# Revit family: 306_eeb4c68d981f462b976296043c77c6
name_source: partatom
category: Pipe Accessories
units: mm (PartAtom-declared; Revit-internal decimal feet)

## family parameters
Always vertical = Yes
Cut with Voids When Loaded = No
Part Type = Valve - Breaks Into
Round Connector Dimension = Use Diameter
Shared = No
Work Plane-Based = No

## types (2) — shared parameters
CAT0 = Yes
Description = 3-way Motorized ball valve MBA136, PN32 internal/2x external thread
H1 = 1 mm  [stored 0.00328084 ft]
L2D_Min = 3048 mm
MC = No
Manufacturer = ESBE
QmdConnectorList = 301;D;302;D
RR = 4 mm  [stored 0.0131234 ft]
URL = http://www.esbe.eu
X14 = 3 mm  [stored 0.00984252 ft]
X15 = 8 mm  [stored 0.0262467 ft]
X15__ve = -8 mm
X16 = 5 mm  [stored 0.0164042 ft]
X5 = 3 mm  [stored 0.00984252 ft]
X5__ve = -3 mm
Y0 = 5 mm  [stored 0.0164042 ft]
Y11 = 3 mm  [stored 0.00984252 ft]
Z3 = 10 mm  [stored 0.0328084 ft]
Z4 = 55 mm
Z5 = 3 mm  [stored 0.00984252 ft]
Z6 = 35 mm
Z6__ve = -35 mm
magiPartTypeId = 306
magiProductFamilyId = eeb4c68d981f462b976296043c77c6

## per-type parameters (varying)
- MBA136 G1  MFM 230VAC 2-P 10NM: CenSd_Y13_6=15 mm  [stored 0.0492126 ft]; D=25 mm; E=29 mm  [stored 0.0951444 ft]; G=76 mm; H=73 mm; L2D=107 mm; W2D=25 mm  [stored 0.082021 ft]; X1=58 mm; X12=19 mm; X12__ve=-19 mm; X13=7 mm  [stored 0.0229659 ft]; X18=52 mm; X19=20 mm  [stored 0.0656168 ft]; X19__ve=-20 mm; X6=21 mm; Y1=13 mm  [stored 0.0426509 ft]; Y10=16 mm; Y10__ve=-16 mm  [stored -0.0524934 ft]; Y12=14 mm  [stored 0.0459318 ft]; Y13=18 mm; Y14=9 mm  [stored 0.0295276 ft]; Y15=17 mm; Y2=13 mm  [stored 0.0426509 ft]; Y3=13 mm  [stored 0.0426509 ft]; Y4=15 mm  [stored 0.0492126 ft]; Y5=15 mm  [stored 0.0492126 ft]; Z10=34 mm; Z2=26 mm; Z2__ve=-26 mm; Z8=16 mm; magiProductCode=MBA136 G1" MFM 230VAC 2-P 10NM; magiProductId=84465b65f17d4973b765fd3aec1b71
- MBA136 G3/4  MFM 230VAC 2-P 10NM: CenSd_Y13_6=12 mm  [stored 0.0393701 ft]; D=20 mm; E=25 mm  [stored 0.082021 ft]; G=70 mm; H=65 mm; L2D=91 mm; W2D=20 mm  [stored 0.0656168 ft]; X1=50 mm  [stored 0.164042 ft]; X12=16 mm; X12__ve=-16 mm  [stored -0.0524934 ft]; X13=6 mm  [stored 0.019685 ft]; X18=45 mm; X19=17 mm; X19__ve=-17 mm; X6=19 mm; Y1=10 mm  [stored 0.0328084 ft]; Y10=13 mm  [stored 0.0426509 ft]; Y10__ve=-13 mm  [stored -0.0426509 ft]; Y12=11 mm; Y13=14 mm  [stored 0.0459318 ft]; Y14=7 mm  [stored 0.0229659 ft]; Y15=13 mm  [stored 0.0426509 ft]; Y2=10 mm  [stored 0.0328084 ft]; Y3=11 mm; Y4=12 mm  [stored 0.0393701 ft]; Y5=12 mm  [stored 0.0393701 ft]; Z10=31 mm; Z2=23 mm; Z2__ve=-23 mm; Z8=15 mm  [stored 0.0492126 ft]; magiProductCode=MBA136 G3/4" MFM 230VAC 2-P 10NM; magiProductId=bc756bae89894fe3935c1dae97aa52

note: [stored X ft] marks values corroborated as IEEE doubles in the binary element streams (Revit-internal decimal feet)

## geometry (parser evidence)
native form markers: Sweep x3
no freeform markers — native parametric forms only
